# Revit family: EL_Marut_S
name_source: partatom
category: Lighting Fixtures
units: mm (PartAtom-declared; Revit-internal decimal feet)

## family parameters
Always vertical = Yes
Cut with Voids When Loaded = No
Light Source = Yes
Maintain Annotation Orientation = No
OmniClass Number = 23.80.70.00
OmniClass Title = Lighting
Part Type = Normal
Room Calculation Point = No
Round Connector Dimension = Use Diameter
Shared = No
Work Plane-Based = No

## types (57) — shared parameters
CE Conformity = CE Mark
Certification = ENEC, ENEC+, EMC, Zhaga D4i, IDA
Color Filter = 16777215
Control Gear = LED Driver
Default Elevation = 1500 mm  [stored 4.92126 ft]
Description = Street luminaire
Diffuser Material  = Flat glass
Dimming Lamp Color Temperature Shift = <None>
EL_Voltage = AC 220V - 240V / 50-60Hz
Housing Height = 99 mm  [stored 0.324803 ft]
Housing Length = 433 mm
Housing Width = 260 mm  [stored 0.853018 ft]
IK = IK 09 / IK10
IP = IP66
Lamp = LED
Life Time = 120 000 h
Light Source Symbol Length = 3048 mm  [stored 10 ft]
Luminaire Material = Kov
Luminaire Type = MARUT S G2
Manufacturer = ELEKTRO-LUMEN, s. r. o.
Model = MARUT S G2
Spot Beam Angle = 30.00°
Spot Field Angle = 90.00°
Terminal Block Poles = 2, 3, 5
Tilt Angle = 90.00°
URL Luminaire = https://www.el-lumen.cz
URL Manufacturer = https://www.el-lumen.cz
Voltage  = AC 220V - 240V / 50-60Hz
Weight = 4

## per-type parameters (varying)
| type | CCT | CRI | Luminous Flux of LED | Luminous Flux of Luminaire | Optic | Optical Efficacy | Power |
| MARUT S G2 Mxx 9k0 740 | 4000 | 70 | 9000 lm | 7802 lm | M03 | 86.69 | 55 W |
| MARUT S G2 Mxx 8k0 740 | 4000 | 70 | 8000 lm | 6935 lm | M03 | 86.69 | 48 W |
| MARUT S G2 Mxx 7k0 740 | 4000 | 70 | 7000 lm | 6068 lm | M03 | 86.69 | 41 W |
| MARUT S G2 Mxx 6k0 740 | 4000 | 70 | 6000 lm | 5201 lm | M03 | 86.69 | 37 W |
| MARUT S G2 Mxx 5k0 740 | 4000 | 70 | 5000 lm | 4335 lm | M03 | 86.69 | 31 W |
| MARUT S G2 Mxx 4k0 740 | 4000 | 70 | 4000 lm | 3468 lm | M03 | 86.69 | 24 W |
| MARUT S G2 Mxx 3k5 740 | 4000 | 70 | 3500 lm | 3034 lm | M03 | 86.69 | 21 W |
| MARUT S G2 Mxx 3k0 740 | 4000 | 70 | 3000 lm | 2601 lm | M03 | 86.69 | 18 W |
| MARUT S G2 Mxx 2k5 740 | 4000 | 70 | 2500 lm | 2167 lm | M03 | 86.69 | 15 W |
| MARUT S G2 Mxx 2k0 740 | 4000 | 70 | 2000 lm | 1734 lm | M03 | 86.69 | 12 W |
| MARUT S G2 Mxx 1k5 740 | 4000 | 70 | 1500 lm | 1300 lm | M03 | 86.69 | 9 W |
| MARUT S G2 Mxx 1k0 740 | 4000 | 70 | 1000 lm | 867 lm | M03 | 86.69 | 7 W |
| MARUT S G2 Mxx 9k0 730 | 3000 | 70 | 9000 lm | 7802 lm | M03 | 86.69 | 59 W |
| MARUT S G2 Mxx 8k0 730 | 3000 | 70 | 8000 lm | 6935 lm | M03 | 86.69 | 51 W |
| MARUT S G2 Mxx 7k0 730 | 3000 | 70 | 7000 lm | 6068 lm | M03 | 86.69 | 44 W |
| MARUT S G2 Mxx 6k0 730 | 3000 | 70 | 6000 lm | 5201 lm | M03 | 86.69 | 40 W |
| MARUT S G2 Mxx 5k0 730 | 3000 | 70 | 5000 lm | 4335 lm | M03 | 86.69 | 32 W |
| MARUT S G2 Mxx 4k0 730 | 3000 | 70 | 4000 lm | 3468 lm | M03 | 86.69 | 25 W |
| MARUT S G2 Mxx 3k5 730 | 3000 | 70 | 3500 lm | 3034 lm | M03 | 86.69 | 22 W |
| MARUT S G2 Mxx 3k0 730 | 3000 | 70 | 3000 lm | 2601 lm | M03 | 86.69 | 18 W |
| MARUT S G2 Mxx 2k5 730 | 3000 | 70 | 2500 lm | 2167 lm | M03 | 86.69 | 15 W |
| MARUT S G2 Mxx 2k0 730 | 3000 | 70 | 2000 lm | 1734 lm | M03 | 86.69 | 12 W |
| MARUT S G2 Mxx 1k5 730 | 3000 | 70 | 1500 lm | 1300 lm | M03 | 86.69 | 10 W |
| MARUT S G2 Mxx 1k0 730 | 3000 | 70 | 1000 lm | 867 lm | M03 | 86.69 | 7 W |
| MARUT S G2 Mxx 9k0 727 | 2700 | 70 | 9000 lm | 7802 lm | M03 | 86.69 | 63 W |
| MARUT S G2 Mxx 8k0 727 | 2700 | 70 | 8000 lm | 6935 lm | M03 | 86.69 | 54 W |
| MARUT S G2 Mxx 7k0 727 | 2700 | 70 | 7000 lm | 6068 lm | M03 | 86.69 | 46 W |
| MARUT S G2 Mxx 6k0 727 | 2700 | 70 | 6000 lm | 5201 lm | M03 | 86.69 | 43 W |
| MARUT S G2 Mxx 5k0 727 | 2700 | 70 | 5000 lm | 4335 lm | M03 | 86.69 | 34 W |
| MARUT S G2 Mxx 4k0 727 | 2700 | 70 | 4000 lm | 3468 lm | M03 | 86.69 | 27 W |
| MARUT S G2 Mxx 3k5 727 | 2700 | 70 | 3500 lm | 3034 lm | M03 | 86.69 | 23 W |
| MARUT S G2 Mxx 3k0 727 | 2700 | 70 | 3000 lm | 2601 lm | M03 | 86.69 | 20 W |
| MARUT S G2 Mxx 2k5 727 | 2700 | 70 | 2500 lm | 2167 lm | M03 | 86.69 | 16 W |
| MARUT S G2 Mxx 2k0 727 | 2700 | 70 | 2000 lm | 1734 lm | M03 | 86.69 | 13 W |
| MARUT S G2 Mxx 1k5 727 | 2700 | 70 | 1500 lm | 1300 lm | M03 | 86.69 | 10 W |
| MARUT S G2 Mxx 1k0 727 | 2700 | 70 | 1000 lm | 867 lm | M03 | 86.69 | 7 W |
| MARUT S G2 Mxx 7k0 722 | 2200 | 70 | 7000 lm | 6068 lm | M03 | 86.69 | 54 W |
| MARUT S G2 Mxx 6k0 722 | 2200 | 70 | 6000 lm | 5201 lm | M03 | 86.69 | 45 W |
| MARUT S G2 Mxx 5k0 722 | 2200 | 70 | 5000 lm | 4335 lm | M03 | 86.69 | 40 W |
| MARUT S G2 Mxx 4k0 722 | 2200 | 70 | 4000 lm | 3468 lm | M03 | 86.69 | 31 W |
| MARUT S G2 Mxx 3k5 722 | 2200 | 70 | 3500 lm | 3034 lm | M03 | 86.69 | 26 W |
| MARUT S G2 Mxx 3k0 722 | 2200 | 70 | 3000 lm | 2601 lm | M03 | 86.69 | 23 W |
| MARUT S G2 Mxx 2k5 722 | 2200 | 70 | 2500 lm | 2167 lm | M03 | 86.69 | 18 W |
| MARUT S G2 Mxx 2k0 722 | 2200 | 70 | 2000 lm | 1734 lm | M03 | 86.69 | 15 W |
| MARUT S G2 Mxx 1k5 722 | 2200 | 70 | 1500 lm | 1300 lm | M03 | 86.69 | 12 W |
| MARUT S G2 Mxx 1k0 722 | 2200 | 70 | 1000 lm | 867 lm | M03 | 86.69 | 8 W |
| MARUT S G2 Lxx 8k0 AMB | 1850 | 50 | 8000 lm | 7226 lm | L03 | 90.32 | 57 W |
| MARUT S G2 Lxx 7k0 AMB | 1850 | 50 | 7000 lm | 6322 lm | L03 | 90.32 | 48 W |
| MARUT S G2 Lxx 6k0 AMB | 1850 | 50 | 6000 lm | 5419 lm | L03 | 90.32 | 41 W |
| MARUT S G2 Lxx 5k0 AMB | 1850 | 50 | 5000 lm | 4516 lm | L03 | 90.32 | 36 W |
| MARUT S G2 Lxx 4k0 AMB | 1850 | 50 | 4000 lm | 3613 lm | L03 | 90.32 | 28 W |
| MARUT S G2 Lxx 3k5 AMB | 1850 | 50 | 3500 lm | 3161 lm | L03 | 90.32 | 25 W |
| MARUT S G2 Lxx 3k0 AMB | 1850 | 50 | 3000 lm | 2710 lm | L03 | 90.32 | 21 W |
| MARUT S G2 Lxx 2k5 AMB | 1850 | 50 | 2500 lm | 2258 lm | L03 | 90.32 | 18 W |
| MARUT S G2 Lxx 2k0 AMB | 1850 | 50 | 2000 lm | 1806 lm | L03 | 90.32 | 14 W |
| MARUT S G2 Lxx 1k5 AMB | 1850 | 50 | 1500 lm | 1355 lm | L03 | 90.32 | 11 W |
| MARUT S G2 Lxx 1k0 AMB | 1850 | 50 | 1000 lm | 903 lm | L03 | 90.32 | 8 W |

note: column(s) folded — value = type name in every type: Luminaire Model

note: [stored X ft] marks values corroborated as IEEE doubles in the binary element streams (Revit-internal decimal feet)
